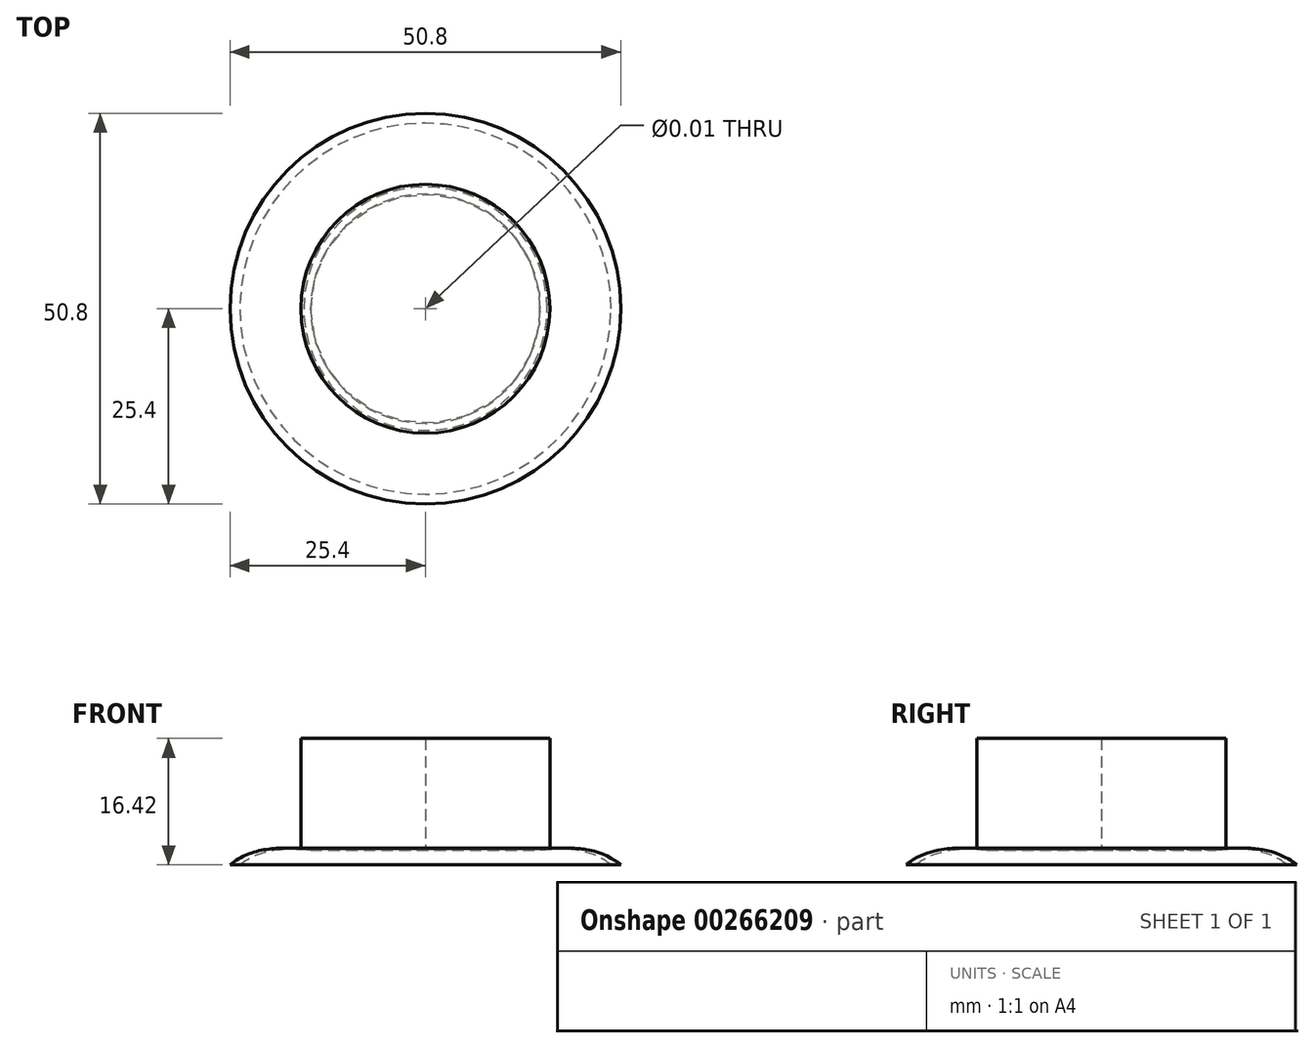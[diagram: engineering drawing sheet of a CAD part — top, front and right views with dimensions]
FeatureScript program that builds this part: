
annotation { "Feature Type Name" : "Feature", "Feature Type Description" : "" }
export const myFeature = defineFeature(function(context is Context, id is Id, definition is map)
    precondition{}
    {
        {
            var Q0;
            Q0=qCreatedBy(makeId("Front.planeOp"),FACE);
            var sketch = newSketch(context, id + "F0", { "sketchPlane" : qUnion([Q0])});
            skLineSegment(sketch, "E0", {"start": v(0, 0) * mm, "end": v(0, -101.6) * mm});
            skLineSegment(sketch, "E1", {"start": v(0, -101.6) * mm, "end": v(25.4, -101.6) * mm});
            skLineSegment(sketch, "E2", {"start": v(25.4, -101.6) * mm, "end": v(-25.4, -101.6) * mm});
            skLineSegment(sketch, "E3", {"start": v(0, 0) * mm, "end": v(0, 50.8) * mm});
            skLineSegment(sketch, "E4", {"start": v(0, 50.8) * mm, "end": v(-25.4, 50.8) * mm});
            skLineSegment(sketch, "E5", {"start": v(-25.4, 50.8) * mm, "end": v(25.4, 50.8) * mm});
            skFitSpline(sketch, "E6", {"points": [v(-25.4, -101.6) * mm, v(-25.4, 50.8) * mm, v(0, 50.8) * mm, v(25.4, 50.8) * mm, v(25.4, -101.6) * mm], "startDerivative": vector(-62.22, 593.54) * mm, "endDerivative": vector(-62.22, -593.54) * mm});
            skLineSegment(sketch, "E7", {"start": v(0, 50.8) * mm, "end": v(-24.13, 50.8) * mm});
            skLineSegment(sketch, "E8", {"start": v(0, 50.8) * mm, "end": v(24.13, 50.8) * mm});
            skLineSegment(sketch, "E9", {"start": v(0, -101.6) * mm, "end": v(-24.13, -101.6) * mm});
            skLineSegment(sketch, "E10", {"start": v(-24.13, -101.6) * mm, "end": v(0, -101.6) * mm});
            skLineSegment(sketch, "E11", {"start": v(0, -101.6) * mm, "end": v(24.13, -101.6) * mm});
            skFitSpline(sketch, "E12", {"points": [v(-24.13, -101.6) * mm, v(-24.13, 50.8) * mm, v(0, 50.8) * mm, v(24.13, 50.8) * mm, v(24.13, -101.6) * mm], "startDerivative": vector(-60.64, 590.16) * mm, "endDerivative": vector(-60.64, -590.16) * mm});
            skLineSegment(sketch, "E13", {"start": v(-24.42, -98.77) * mm, "end": v(24.42, -98.77) * mm});
            skLineSegment(sketch, "E14", {"start": v(0, 68.82) * mm, "end": v(0, 67.22) * mm});
            skPoint(sketch, "E14.startSnap0", {"position": v(0, 67.22) * mm});
            skPoint(sketch, "E14.endSnap0", {"position": v(0, 67.22) * mm});
            skLineSegment(sketch, "E15.bottom", {"start": v(16.18, 52.83) * mm, "end": v(0, 52.83) * mm});
            skLineSegment(sketch, "E15.top", {"start": v(16.18, 67.22) * mm, "end": v(0, 67.22) * mm});
            skLineSegment(sketch, "E15.left", {"start": v(16.18, 52.83) * mm, "end": v(16.18, 67.22) * mm});
            skLineSegment(sketch, "E15.right", {"start": v(0, 52.83) * mm, "end": v(0, 67.22) * mm});
            skSolve(sketch);
        }
        {
            var Q0;
            {var subQ0=sQuery(id+"F0.wireOp",EDGE,"E6");var subQ5=makeQuery(id+"F0.imprint","INTERSECT",VERTEX,{"derivedFrom":[subQ0,sQuery(id+"F0.wireOp",EDGE,"E3Ss95oR-lK0A-xV8t-yU9l-XVISUjezfQUN")]});Q0=makeQuery(id+"F0.imprint","IMPRINT",FACE,{"disambiguationData":[TD([[makeQuery(id+"F0.imprint","IMPRINT",EDGE,{"disambiguationData":[TD([[subQ5,1.0]])],"derivedFrom":subQ0}),-1.0]])]});}
            var Q1;
            {var subQ4=sQuery(id+"F0.wireOp",EDGE,"E6");var subQ5=sQuery(id+"F0.wireOp",EDGE,"E2");var subQ6=makeQuery(id+"F0.imprint","INTERSECT",VERTEX,{"disambiguationData":[OD(0.0)],"derivedFrom":[subQ5,subQ4]});Q1=makeQuery(id+"F0.imprint","IMPRINT",FACE,{"disambiguationData":[TD([[makeQuery(id+"F0.imprint","IMPRINT",EDGE,{"disambiguationData":[TD([[subQ6,1.0]])],"derivedFrom":subQ4}),-1.0]])]});}
            var Q2;
            {var subQ0=sQuery(id+"F0.wireOp",EDGE,"E11");Q2=makeQuery(id+"F0.imprint","IMPRINT",FACE,{"disambiguationData":[TD([[makeQuery(id+"F0.imprint","IMPRINT",EDGE,{"derivedFrom":subQ0}),1.0]])]});}
            var Q3;
            Q3=sQuery(id+"F0.wireOp",EDGE,"E3");
            revolve(context, id + "F1", {"entities" : qUnion([Q0, Q1, Q2]), "axis" : qUnion([Q3]), "revolveType" : RevolveType.FULL});
        }
        {
            var Q0;
            {var subQ1=sQuery(id+"F0.wireOp",EDGE,"E15.top");Q0=makeQuery(id+"F0.imprint","IMPRINT",FACE,{"disambiguationData":[TD([[makeQuery(id+"F0.imprint","IMPRINT",EDGE,{"derivedFrom":subQ1}),1.0]])]});}
            var Q1;
            Q1=sQuery(id+"F0.wireOp",EDGE,"E3");
            revolve(context, id + "F2", {"entities" : qUnion([Q0]), "axis" : qUnion([Q1]), "revolveType" : RevolveType.FULL});
        }
    });
